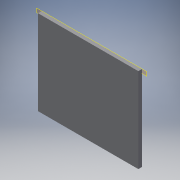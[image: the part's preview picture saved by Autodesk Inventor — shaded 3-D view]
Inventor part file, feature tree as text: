
AUTODESK INVENTOR PART (.ipt)
format: ipt  version: 2018 (Build 220112000, 112)  size: 103,936 bytes
history: native  units: in
note: dims shown in document units (in); Inventor stores cm internally (conversion verified against a paired STEP export)
features: other x3, sketch x2, plane x1, extrude x1, projected_geometry x1
ambient origin geometry x8: Origin, YZ Plane, XZ Plane, XY Plane, X Axis, Y Axis, Z Axis, Center Point
bodies: Solid1 (feature_tree)
feature tree (8):
  plane  "Work Plane1"
  extrude  "Extrusion1"  [1 undecoded]
  sketch  "Sketch2"
  sketch  "Sketch1"  dims[d0=0.1575in d1=0.0in]
  projected_geometry  "Projected Loop1"
  other  "<userpath>\Documents\GitHub\caja-reductora-II\CAJA_FUENTE_ENSAMBLE.iam"
  other  "CAJA_FUENTE_ENSAMBLE.iam"
  other  "FUENTE 1:2"
note: 1 required parameter value undecoded (feature->parameter linkage not recoverable at this tier; creation-order binding heuristic only, values carry confidence <= 0.55)
